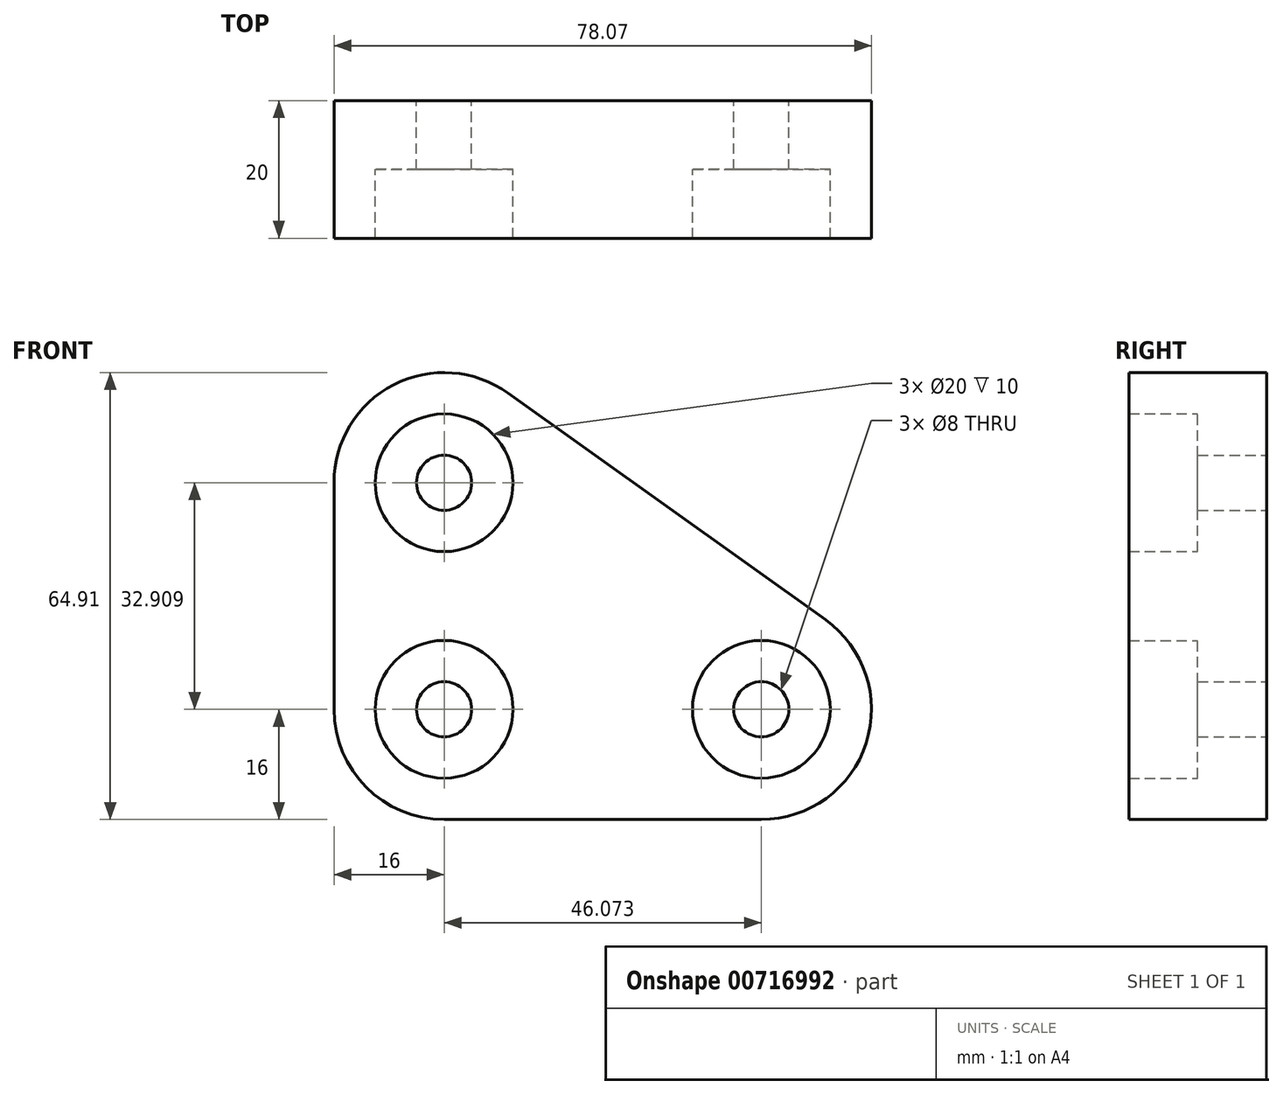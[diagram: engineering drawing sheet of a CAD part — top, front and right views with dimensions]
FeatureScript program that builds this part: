
annotation { "Feature Type Name" : "Feature", "Feature Type Description" : "" }
export const myFeature = defineFeature(function(context is Context, id is Id, definition is map)
    precondition{}
    {
        {
            var Q0;
            Q0=qCreatedBy(makeId("Front.planeOp"),FACE);
            var sketch = newSketch(context, id + "F0", { "sketchPlane" : qUnion([Q0])});
            skLineSegment(sketch, "E0.bottom", {"start": v(16, 0) * mm, "end": v(62.07, 0) * mm});
            skLineSegment(sketch, "E0.left", {"start": v(0, 16) * mm, "end": v(0, 48.9) * mm});
            skLineSegment(sketch, "E1", {"start": v(25.3, 61.93) * mm, "end": v(71.37, 29.02) * mm});
            skPoint(sketch, "E2.visualSharp", {"position": v(0, 80) * mm});
            skArc(sketch, "E2.filletArc", {"start": v(25.3, 61.93) * mm, "mid": v(8.68, 63.14) * mm, "end": v(0, 48.9) * mm});
            skPoint(sketch, "E3.visualSharp", {"position": v(0, 0) * mm});
            skArc(sketch, "E3.filletArc", {"start": v(0, 16) * mm, "mid": v(4.69, 4.69) * mm, "end": v(16, 0) * mm});
            skPoint(sketch, "E4.visualSharp", {"position": v(112, 0) * mm});
            skArc(sketch, "E4.filletArc", {"start": v(62.07, 0) * mm, "mid": v(77.3, 11.12) * mm, "end": v(71.37, 29.02) * mm});
            skCircle(sketch, "E5", {"center": v(16, 48.9) * mm, "radius": 10 * mm});
            skCircle(sketch, "E6", {"center": v(16, 16) * mm, "radius": 10 * mm});
            skCircle(sketch, "E7", {"center": v(62.07, 16) * mm, "radius": 10 * mm});
            skCircle(sketch, "E8", {"center": v(16, 48.9) * mm, "radius": 4 * mm});
            skCircle(sketch, "E9", {"center": v(16, 16) * mm, "radius": 4 * mm});
            skCircle(sketch, "E10", {"center": v(62.07, 16) * mm, "radius": 4 * mm});
            skSolve(sketch);
        }
        {
            var Q0;
            Q0=makeQuery(id+"F0.imprint","IMPRINT",FACE,{"disambiguationData":[TD([[makeQuery(id+"F0.imprint","IMPRINT",EDGE,{"derivedFrom":sQuery(id+"F0.wireOp",EDGE,"E0.bottom")}),1.0]])]});
            extrude(context, id + "F1", {"entities" : qUnion([Q0]), "depth" : 20 * mm, "offsetDistance" : 25 * mm});
        }
        {
            var Q0;
            Q0=makeQuery(id+"F0.imprint","IMPRINT",FACE,{"disambiguationData":[TD([[makeQuery(id+"F0.imprint","IMPRINT",EDGE,{"derivedFrom":sQuery(id+"F0.wireOp",EDGE,"E6")}),1.0]])]});
            var Q1;
            Q1=makeQuery(id+"F0.imprint","IMPRINT",FACE,{"disambiguationData":[TD([[makeQuery(id+"F0.imprint","IMPRINT",EDGE,{"derivedFrom":sQuery(id+"F0.wireOp",EDGE,"E5")}),1.0]])]});
            var Q2;
            Q2=makeQuery(id+"F0.imprint","IMPRINT",FACE,{"disambiguationData":[TD([[makeQuery(id+"F0.imprint","IMPRINT",EDGE,{"derivedFrom":sQuery(id+"F0.wireOp",EDGE,"E7")}),1.0]])]});
            extrude(context, id + "F2", {"entities" : qUnion([Q0, Q1, Q2]), "operationType" : NewBodyOperationType.ADD, "depth" : 10 * mm, "offsetDistance" : 25 * mm});
        }
    });
